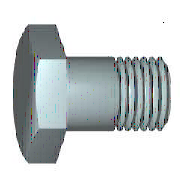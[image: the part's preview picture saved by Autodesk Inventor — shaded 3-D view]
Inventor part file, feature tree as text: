
AUTODESK INVENTOR PART (.ipt)
format: ipt  version: 2025 (Build 290162000, 162)  size: 192,000 bytes
history: native  units: mm (DEFAULTED — no unit token found)
features: other x1, extrude x1, chamfer x1, plane x1
ambient origin geometry x7: Origin, YZ Plane, XZ Plane, X Axis, Y Axis, Z Axis, Center Point
bodies: Solid1 (feature_tree)
feature tree (4):
  other  "轴承体"
  extrude  "头"  Depth=100.0mm
  chamfer  "倒角1"  Distance=30.0mm
  plane  "Work Plane1"
